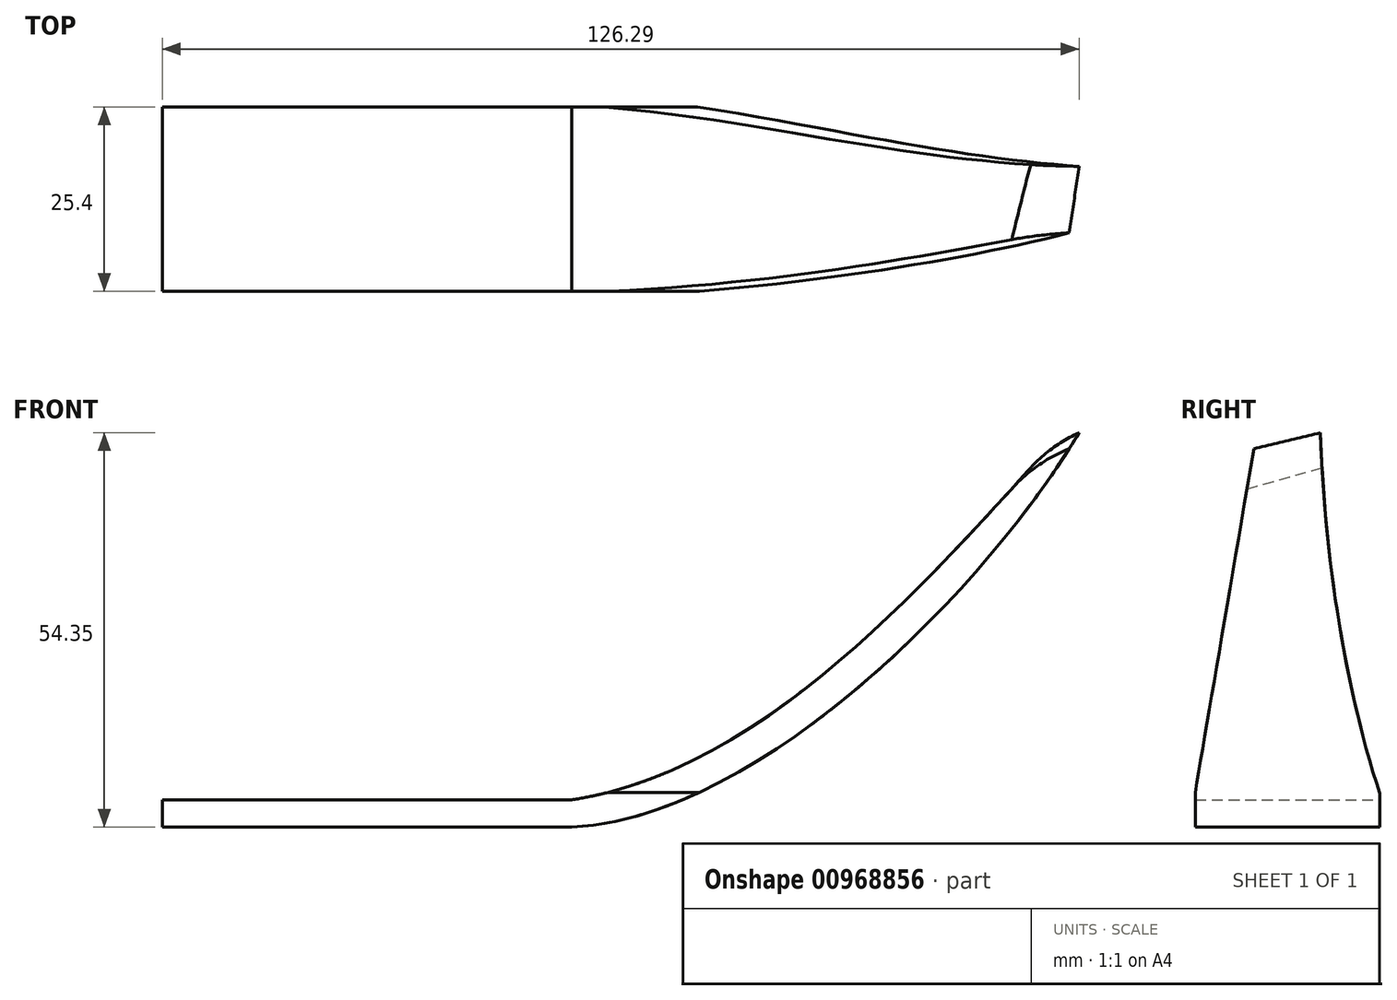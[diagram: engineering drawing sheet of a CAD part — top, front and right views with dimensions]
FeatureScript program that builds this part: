
annotation { "Feature Type Name" : "Feature", "Feature Type Description" : "" }
export const myFeature = defineFeature(function(context is Context, id is Id, definition is map)
    precondition{}
    {
        {
            var Q0;
            Q0=qCreatedBy(makeId("Front.planeOp"),FACE);
            var sketch = newSketch(context, id + "F0", { "sketchPlane" : qUnion([Q0])});
            skLineSegment(sketch, "E0", {"start": v(-56.38, 7.4) * mm, "end": v(0, 7.4) * mm});
            skFitSpline(sketch, "E1", {"points": [v(0, 7.4) * mm, v(73.29, 64.12) * mm], "startDerivative": vector(89.93, 13.47) * mm, "endDerivative": vector(55.08, 58.08) * mm});
            skLineSegment(sketch, "E2.2", {"start": v(-56.39, 3.63) * mm, "end": v(0, 3.63) * mm});
            skFitSpline(sketch, "E3", {"points": [v(73.29, 64.12) * mm, v(0, 3.63) * mm], "startDerivative": vector(-34.23, -69.38) * mm, "endDerivative": vector(-82.76, -3.96) * mm});
            skLineSegment(sketch, "E4", {"start": v(-56.38, 7.4) * mm, "end": v(-56.39, 3.63) * mm});
            skSolve(sketch);
        }
        {
            var Q0;
            Q0=makeQuery(id+"F0.imprint","IMPRINT",FACE,{"disambiguationData":[TD([[makeQuery(id+"F0.imprint","IMPRINT",EDGE,{"derivedFrom":sQuery(id+"F0.wireOp",EDGE,"E0")}),-1.0]])]});
            extrude(context, id + "F1", {"entities" : qUnion([Q0]), "endBound" : BoundingType.SYMMETRIC, "depth" : 25.4 * mm, "offsetDistance" : 25.4 * mm});
        }
        {
            var Q0;
            Q0=qCreatedBy(makeId("Right.planeOp"),FACE);
            cPlane(context, id + "F2", {"entities" : qUnion([Q0]), "cplaneType" : CPlaneType.OFFSET, "offset" : 3.3 * mm, "width" : 152.4 * mm, "height" : 152.4 * mm});
        }
        {
            var Q0;
            Q0=qCreatedBy(id+"F2.planeOp",FACE);
            var sketch = newSketch(context, id + "F3", { "sketchPlane" : qUnion([Q0])});
            skFitSpline(sketch, "E5", {"points": [v(12.83, 7.9) * mm, v(4.53, 57.98) * mm], "startDerivative": vector(-14.23, 43.59) * mm, "endDerivative": vector(-2.18, 55.9) * mm});
            skLineSegment(sketch, "E6", {"start": v(18.35, 64.95) * mm, "end": v(18.35, 6.92) * mm});
            skLineSegment(sketch, "E7", {"start": v(18.35, 6.92) * mm, "end": v(12.83, 7.9) * mm});
            skLineSegment(sketch, "E8.MirrorCS", {"start": v(-18.8, 6.92) * mm, "end": v(-12.82, 7.74) * mm});
            skLineSegment(sketch, "E9", {"start": v(-18.57, 64.96) * mm, "end": v(-18.57, 6.95) * mm});
            skLineSegment(sketch, "E10", {"start": v(4.53, 57.98) * mm, "end": v(-4.63, 55.77) * mm});
            skLineSegment(sketch, "E11", {"start": v(18.35, 64.95) * mm, "end": v(-18.57, 64.96) * mm});
            skLineSegment(sketch, "E12", {"start": v(-4.63, 55.77) * mm, "end": v(-12.82, 7.74) * mm});
            skSolve(sketch);
        }
        {
            var Q0;
            Q0=makeQuery(id+"F3.imprint","IMPRINT",FACE,{"disambiguationData":[TD([[makeQuery(id+"F3.imprint","IMPRINT",EDGE,{"derivedFrom":sQuery(id+"F3.wireOp",EDGE,"E5")}),-1.0]])]});
            extrude(context, id + "F4", {"entities" : qUnion([Q0]), "operationType" : NewBodyOperationType.REMOVE, "depth" : 97.8 * mm, "offsetDistance" : 25.4 * mm});
        }
        {
            var Q0;
            Q0=qCreatedBy(makeId("Front.planeOp"),FACE);
            cPlane(context, id + "F5", {"entities" : qUnion([Q0]), "cplaneType" : CPlaneType.OFFSET, "offset" : 12.95 * mm, "width" : 152.4 * mm, "height" : 152.4 * mm});
        }
        {
            var Q0;
            Q0=qCreatedBy(makeId("Front.planeOp"),FACE);
            cPlane(context, id + "F6", {"entities" : qUnion([Q0]), "cplaneType" : CPlaneType.OFFSET, "offset" : 21.34 * mm, "oppositeDirection" : true, "width" : 152.4 * mm, "height" : 152.4 * mm});
        }
        {
            var Q0;
            Q0=makeQuery(id+"F4.boolean.opBoolean","INTERSECT",EDGE,{"derivedFrom":[makeQuery(id+"F1.opExtrude","SWEPT_FACE",FACE,{"disambiguationData":[OSD([sQuery(id+"F0.wireOp",EDGE,"E1")])]}),makeQuery(id+"F4.opExtrude","SWEPT_FACE",FACE,{"disambiguationData":[OSD([sQuery(id+"F3.wireOp",EDGE,"E10")])]})]});
            fillet(context, id + "F7", {"entities" : qUnion([Q0]), "radius" : 17.76 * mm, "tangentPropagation" : true, "allowEdgeOverflow" : false});
        }
    });
